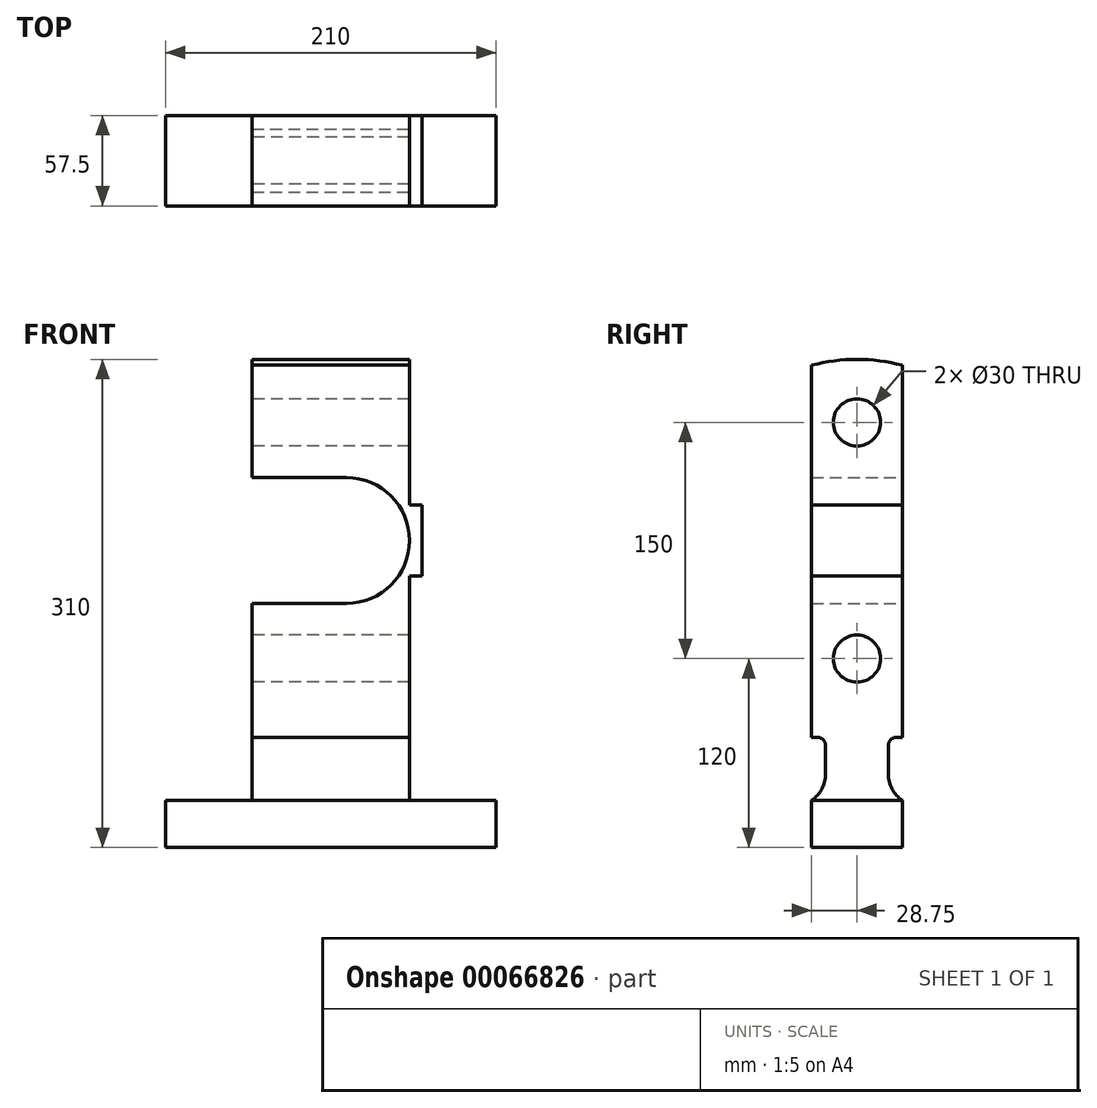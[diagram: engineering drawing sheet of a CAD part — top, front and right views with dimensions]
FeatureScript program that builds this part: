
annotation { "Feature Type Name" : "Feature", "Feature Type Description" : "" }
export const myFeature = defineFeature(function(context is Context, id is Id, definition is map)
    precondition{}
    {
        {
            var Q0;
            Q0=qCreatedBy(makeId("Front.planeOp"),FACE);
            var sketch = newSketch(context, id + "F0", { "sketchPlane" : qUnion([Q0])});
            skLineSegment(sketch, "E0", {"start": v(-105, 0) * mm, "end": v(105, 0) * mm});
            skLineSegment(sketch, "E1", {"start": v(105, 0) * mm, "end": v(105, 30) * mm});
            skLineSegment(sketch, "E2", {"start": v(105, 30) * mm, "end": v(50, 30) * mm});
            skLineSegment(sketch, "E3", {"start": v(50, 30) * mm, "end": v(50, 172.5) * mm});
            skLineSegment(sketch, "E4", {"start": v(50, 172.5) * mm, "end": v(58, 172.5) * mm});
            skLineSegment(sketch, "E5", {"start": v(58, 172.5) * mm, "end": v(58, 217.5) * mm});
            skLineSegment(sketch, "E6", {"start": v(58, 217.5) * mm, "end": v(50, 217.5) * mm});
            skLineSegment(sketch, "E7", {"start": v(50, 217.5) * mm, "end": v(50, 315) * mm});
            skLineSegment(sketch, "E8", {"start": v(50, 315) * mm, "end": v(-50, 315) * mm});
            skLineSegment(sketch, "E9", {"start": v(-50, 315) * mm, "end": v(-50, 235) * mm});
            skLineSegment(sketch, "E10", {"start": v(-50, 30) * mm, "end": v(-105, 30) * mm});
            skLineSegment(sketch, "E11", {"start": v(-105, 30) * mm, "end": v(-105, 0) * mm});
            skArc(sketch, "E12", {"start": v(10, 155) * mm, "mid": v(50, 195) * mm, "end": v(10, 235) * mm});
            skPoint(sketch, "E12.centerSnap0", {"position": v(58, 195) * mm});
            skLineSegment(sketch, "E13", {"start": v(10, 235) * mm, "end": v(-50, 235) * mm});
            skLineSegment(sketch, "E14", {"start": v(10, 155) * mm, "end": v(-50, 155) * mm});
            skLineSegment(sketch, "E15.trimOffspring", {"start": v(-50, 155) * mm, "end": v(-50, 30) * mm});
            skSolve(sketch);
        }
        {
            var Q0;
            Q0=makeQuery(id+"F0.imprint","IMPRINT",FACE,{"disambiguationData":[TD([[makeQuery(id+"F0.imprint","IMPRINT",EDGE,{"derivedFrom":sQuery(id+"F0.wireOp",EDGE,"E0")}),1.0]])]});
            extrude(context, id + "F1", {"entities" : qUnion([Q0]), "endBound" : BoundingType.SYMMETRIC, "depth" : (115 / 2) * mm});
        }
        {
            var Q0;
            Q0=qCreatedBy(makeId("Right.planeOp"),FACE);
            var sketch = newSketch(context, id + "F2", { "sketchPlane" : qUnion([Q0])});
            skLineSegment(sketch, "E16", {"start": v(-129.57, 30) * mm, "end": v(-20, 30) * mm});
            skLineSegment(sketch, "E17", {"start": v(-20, 30) * mm, "end": v(-20, 70) * mm});
            skLineSegment(sketch, "E18", {"start": v(-20, 70) * mm, "end": v(-28.75, 70) * mm});
            skLineSegment(sketch, "E19", {"start": v(-28.75, 70) * mm, "end": v(-28.75, 306.35) * mm});
            skLineSegment(sketch, "E20", {"start": v(28.75, 306.35) * mm, "end": v(28.75, 70) * mm});
            skLineSegment(sketch, "E21", {"start": v(28.75, 70) * mm, "end": v(20, 70) * mm});
            skLineSegment(sketch, "E22", {"start": v(20, 70) * mm, "end": v(20, 30) * mm});
            skLineSegment(sketch, "E23", {"start": v(20, 30) * mm, "end": v(130.78, 30) * mm});
            skLineSegment(sketch, "E24", {"start": v(130.78, 30) * mm, "end": v(130.78, 348.68) * mm});
            skLineSegment(sketch, "E25", {"start": v(130.78, 348.68) * mm, "end": v(-129.57, 348.68) * mm});
            skLineSegment(sketch, "E26", {"start": v(-129.57, 348.68) * mm, "end": v(-129.57, 30) * mm});
            skArc(sketch, "E27.trimOffspring", {"start": v(28.75, 306.35) * mm, "mid": v(0, 310) * mm, "end": v(-28.75, 306.35) * mm});
            skSolve(sketch);
        }
        {
            var Q0;
            Q0=makeQuery(id+"F2.imprint","IMPRINT",FACE,{"disambiguationData":[TD([[makeQuery(id+"F2.imprint","IMPRINT",EDGE,{"derivedFrom":sQuery(id+"F2.wireOp",EDGE,"E16")}),1.0]])]});
            extrude(context, id + "F3", {"entities" : qUnion([Q0]), "operationType" : NewBodyOperationType.REMOVE, "endBound" : BoundingType.THROUGH_ALL, "oppositeDirection" : true, "depth" : 25 * mm, "hasSecondDirection" : true, "secondDirectionBound" : SecondDirectionBoundingType.THROUGH_ALL, "secondDirectionOppositeDirection" : false, "secondDirectionDepth" : 25 * mm});
        }
        {
            var Q0;
            Q0=makeQuery(id+"F3.boolean.opBoolean","COPY",EDGE,{"derivedFrom":makeQuery(id+"F3.opExtrude","SWEPT_EDGE",EDGE,{"disambiguationData":[OSD([sQuery(id+"F2.wireOp",EDGE,"E16"),sQuery(id+"F2.wireOp",EDGE,"E17")])]})});
            var Q1;
            Q1=makeQuery(id+"F3.boolean.opBoolean","COPY",EDGE,{"derivedFrom":makeQuery(id+"F3.opExtrude","SWEPT_EDGE",EDGE,{"disambiguationData":[OSD([sQuery(id+"F2.wireOp",EDGE,"E22"),sQuery(id+"F2.wireOp",EDGE,"E23")])]})});
            fillet(context, id + "F4", {"entities" : qUnion([Q0, Q1]), "radius" : 20 * mm, "tangentPropagation" : true, "allowEdgeOverflow" : false});
        }
        {
            var Q0;
            Q0=makeQuery(id+"F3.boolean.opBoolean","COPY",EDGE,{"derivedFrom":makeQuery(id+"F3.opExtrude","SWEPT_EDGE",EDGE,{"disambiguationData":[OSD([sQuery(id+"F2.wireOp",EDGE,"E21"),sQuery(id+"F2.wireOp",EDGE,"E22")])]})});
            var Q1;
            Q1=makeQuery(id+"F3.boolean.opBoolean","COPY",EDGE,{"derivedFrom":makeQuery(id+"F3.opExtrude","SWEPT_EDGE",EDGE,{"disambiguationData":[OSD([sQuery(id+"F2.wireOp",EDGE,"E17"),sQuery(id+"F2.wireOp",EDGE,"E18")])]})});
            fillet(context, id + "F5", {"entities" : qUnion([Q0, Q1]), "radius" : 5 * mm, "tangentPropagation" : true, "allowEdgeOverflow" : false});
        }
        {
            var Q0;
            Q0=makeQuery(id+"F1.opExtrude","SWEPT_FACE",FACE,{"disambiguationData":[OSD([sQuery(id+"F0.wireOp",EDGE,"E9")])]});
            var sketch = newSketch(context, id + "F6", { "sketchPlane" : qUnion([Q0])});
            skPoint(sketch, "E28", {"position": v(0, 270) * mm});
            skPoint(sketch, "E29", {"position": v(0, 120) * mm});
            skSolve(sketch);
        }
        {
            var Q0;
            Q0=sQuery(id+"F6.wireOp",VERTEX,"E28");
            var Q1;
            Q1=sQuery(id+"F6.wireOp",VERTEX,"E29");
            var Q2;
            Q2=makeQuery(id+"F1.opExtrude","SWEPT_BODY",BODY,{"disambiguationData":[OSD([sQuery(id+"F0.wireOp",EDGE,"E0"),sQuery(id+"F0.wireOp",EDGE,"E1"),sQuery(id+"F0.wireOp",EDGE,"E2"),sQuery(id+"F0.wireOp",EDGE,"E3"),sQuery(id+"F0.wireOp",EDGE,"E4"),sQuery(id+"F0.wireOp",EDGE,"E5"),sQuery(id+"F0.wireOp",EDGE,"E6"),sQuery(id+"F0.wireOp",EDGE,"E7"),sQuery(id+"F0.wireOp",EDGE,"E8"),sQuery(id+"F0.wireOp",EDGE,"E9"),sQuery(id+"F0.wireOp",EDGE,"E10"),sQuery(id+"F0.wireOp",EDGE,"E11"),sQuery(id+"F0.wireOp",EDGE,"E12"),sQuery(id+"F0.wireOp",EDGE,"E13"),sQuery(id+"F0.wireOp",EDGE,"E14"),sQuery(id+"F0.wireOp",EDGE,"E15.trimOffspring")])]});
            hole(context, id + "F7", {"style" : HoleStyle.SIMPLE, "holeDiameter" : 30 * mm, "endStyle" : HoleEndStyle.THROUGH, "locations" : qUnion([Q0, Q1]), "scope" : qUnion([Q2])});
        }
    });
